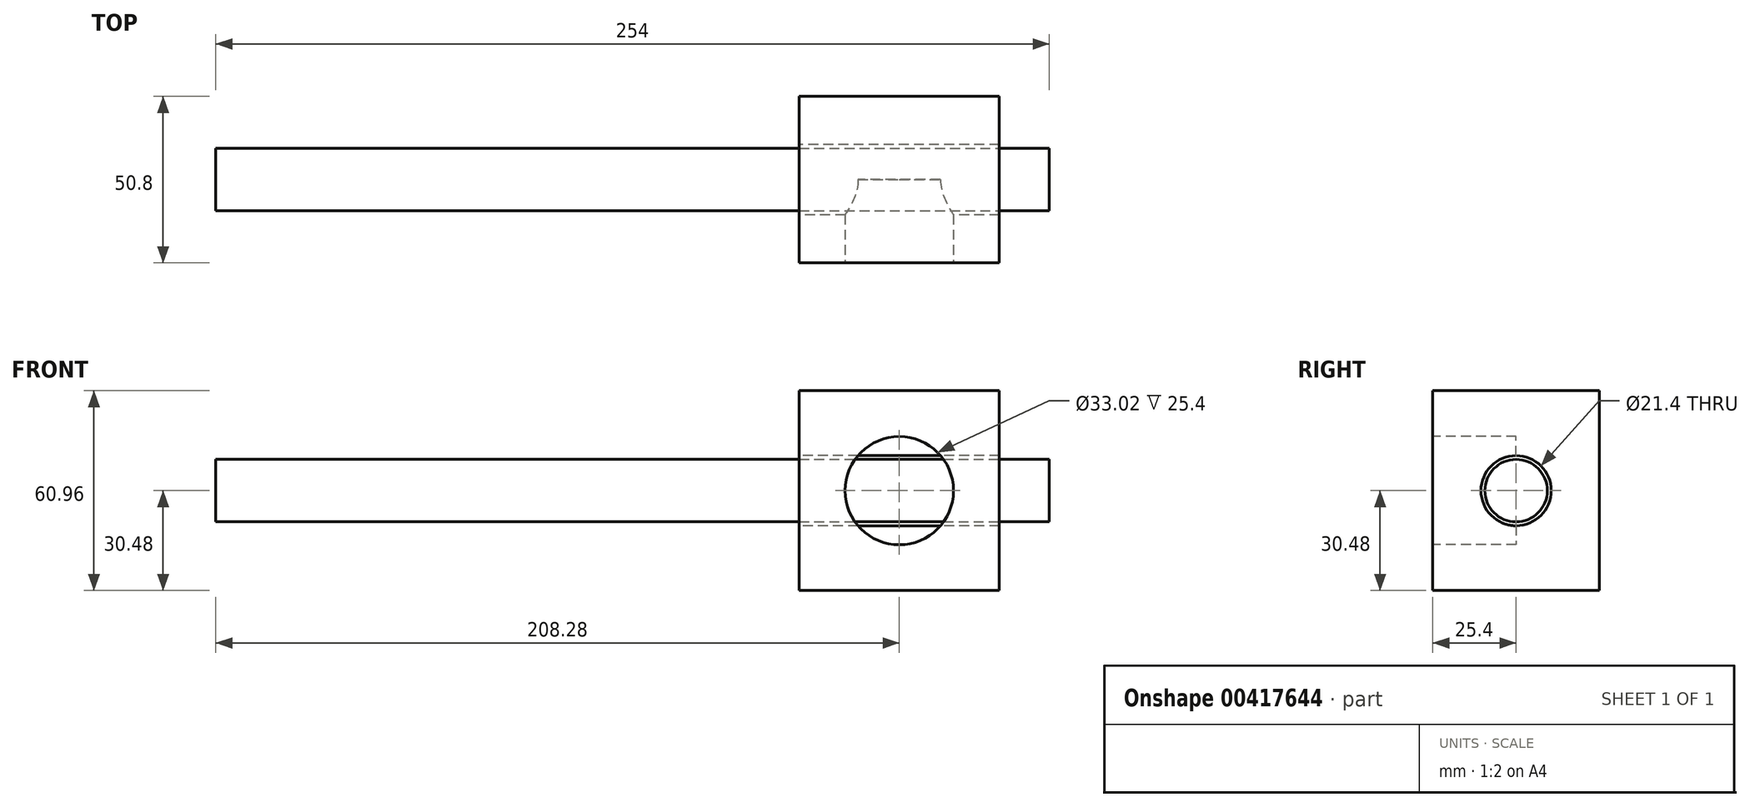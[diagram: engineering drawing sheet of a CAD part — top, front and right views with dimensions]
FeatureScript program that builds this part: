
annotation { "Feature Type Name" : "Feature", "Feature Type Description" : "" }
export const myFeature = defineFeature(function(context is Context, id is Id, definition is map)
    precondition{}
    {
        {
            var Q0;
            Q0=qCreatedBy(makeId("Front.planeOp"),FACE);
            var sketch = newSketch(context, id + "F0", { "sketchPlane" : qUnion([Q0])});
            skLineSegment(sketch, "E0.bottom", {"start": v(0, 0) * mm, "end": v(60.96, 0) * mm});
            skLineSegment(sketch, "E0.top", {"start": v(0, 60.96) * mm, "end": v(60.96, 60.96) * mm});
            skLineSegment(sketch, "E0.left", {"start": v(0, 0) * mm, "end": v(0, 60.96) * mm});
            skLineSegment(sketch, "E0.right", {"start": v(60.96, 0) * mm, "end": v(60.96, 60.96) * mm});
            skSolve(sketch);
        }
        {
            var Q0;
            Q0 = qSketchRegion(id + "F0", true);
            extrude(context, id + "F1", {"entities" : qUnion([Q0]), "depth" : 50.8 * mm});
        }
        {
            var Q0;
            Q0=makeQuery(id+"F1.opExtrude","CAP_FACE",FACE,{"disambiguationData":[OSD([sQuery(id+"F0.wireOp",EDGE,"E0.bottom"),sQuery(id+"F0.wireOp",EDGE,"E0.top"),sQuery(id+"F0.wireOp",EDGE,"E0.left"),sQuery(id+"F0.wireOp",EDGE,"E0.right")])],"isStart":false});
            var sketch = newSketch(context, id + "F2", { "sketchPlane" : qUnion([Q0])});
            skCircle(sketch, "E1", {"center": v(30.48, 30.48) * mm, "radius": 16.51 * mm});
            skSolve(sketch);
        }
        {
            var Q0;
            Q0 = qSketchRegion(id + "F2", true);
            extrude(context, id + "F3", {"entities" : qUnion([Q0]), "operationType" : NewBodyOperationType.REMOVE, "oppositeDirection" : true, "depth" : 25.4 * mm});
        }
        {
            var Q0;
            Q0=makeQuery(id+"F1.opExtrude","SWEPT_FACE",FACE,{"disambiguationData":[OSD([sQuery(id+"F0.wireOp",EDGE,"E0.left")])]});
            var sketch = newSketch(context, id + "F4", { "sketchPlane" : qUnion([Q0])});
            skCircle(sketch, "E2", {"center": v(25.4, 30.48) * mm, "radius": 10.7 * mm});
            skSolve(sketch);
        }
        {
            var Q0;
            Q0 = qSketchRegion(id + "F4", true);
            extrude(context, id + "F5", {"entities" : qUnion([Q0]), "operationType" : NewBodyOperationType.REMOVE, "oppositeDirection" : true, "depth" : 60.96 * mm});
        }
        {
            var Q0;
            Q0=qCreatedBy(makeId("Right.planeOp"),FACE);
            cPlane(context, id + "F6", {"entities" : qUnion([Q0]), "cplaneType" : CPlaneType.OFFSET, "offset" : 76.2 * mm, "width" : 152.4 * mm, "height" : 152.4 * mm});
        }
        {
            var Q0;
            Q0=qCreatedBy(id+"F6.planeOp",FACE);
            var sketch = newSketch(context, id + "F7", { "sketchPlane" : qUnion([Q0])});
            skCircle(sketch, "E3", {"center": v(-25.4, 30.48) * mm, "radius": 9.53 * mm});
            skSolve(sketch);
        }
        {
            var Q0;
            Q0 = qSketchRegion(id + "F7", true);
            extrude(context, id + "F8", {"entities" : qUnion([Q0]), "oppositeDirection" : true, "depth" : 254 * mm});
        }
    });
